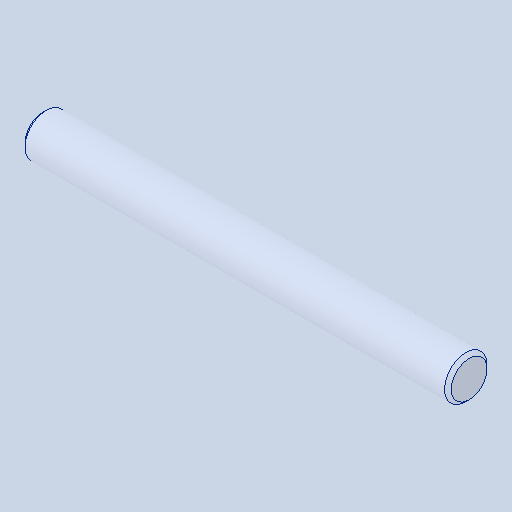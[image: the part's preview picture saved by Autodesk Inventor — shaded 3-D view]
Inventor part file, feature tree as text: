
AUTODESK INVENTOR PART (.ipt)
format: ipt  version: 2023.4 (Build 274418000, 418)  size: 85,504 bytes
history: native  units: in
note: dims shown in document units (in); Inventor stores cm internally (conversion verified against a paired STEP export)
features: chamfer x1
ambient origin geometry x8: Origin, YZ Plane, XZ Plane, XY Plane, X Axis, Y Axis, Z Axis, Center Point
bodies: Solid1 (feature_tree)
feature tree (1):
  chamfer  "Chamfer1"  [1 undecoded]
note: 1 required parameter value undecoded (feature->parameter linkage not recoverable at this tier; creation-order binding heuristic only, values carry confidence <= 0.55)
